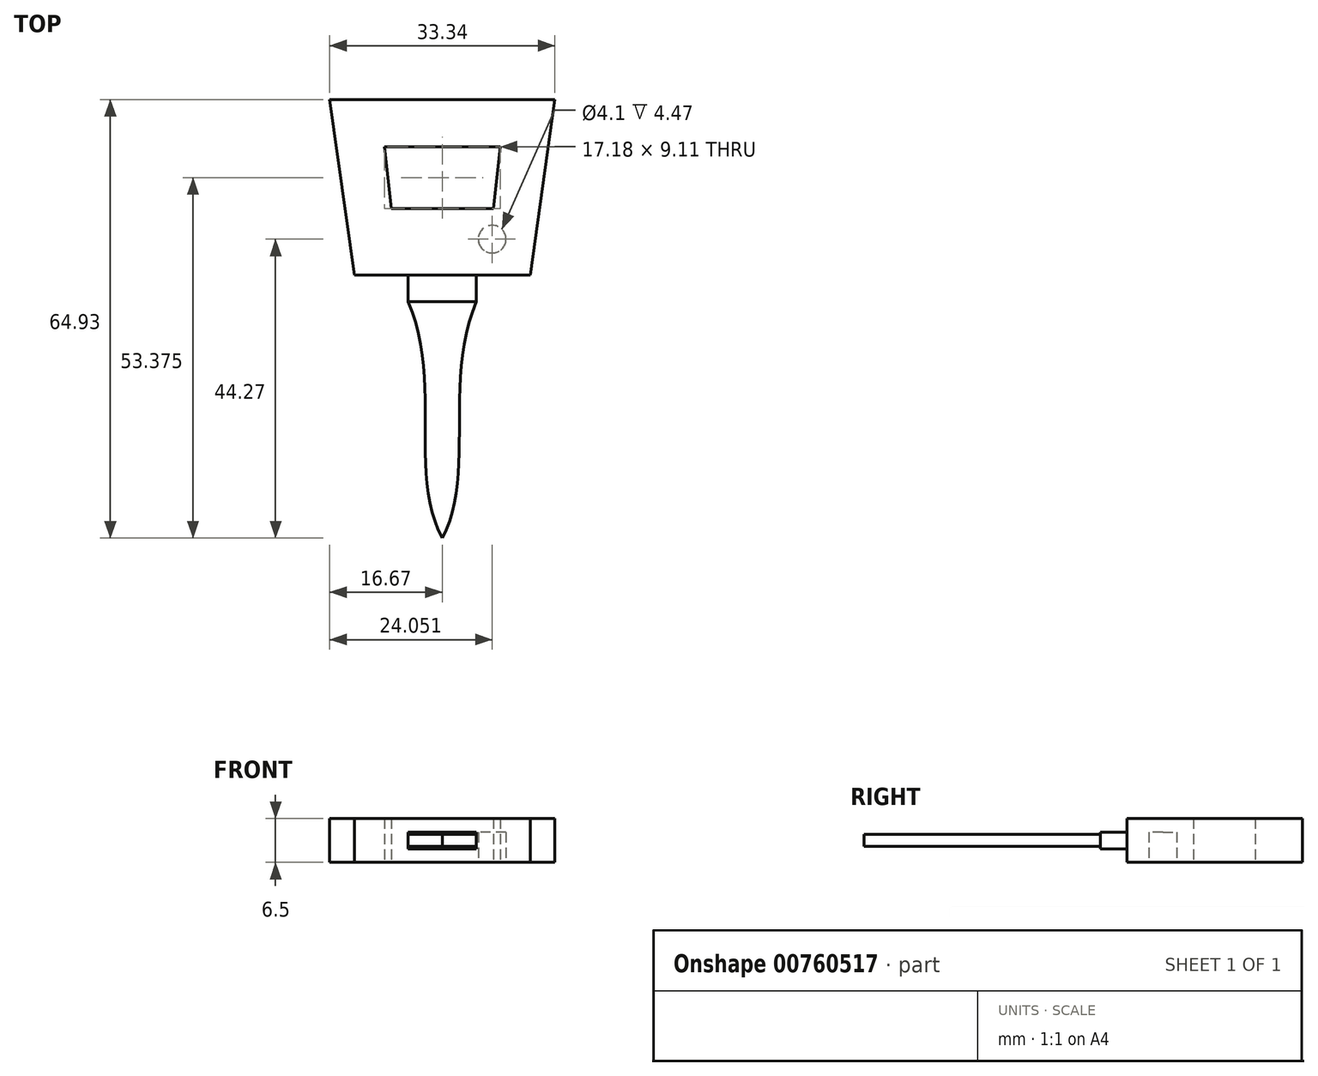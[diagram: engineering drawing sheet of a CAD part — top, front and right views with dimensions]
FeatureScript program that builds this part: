
annotation { "Feature Type Name" : "Feature", "Feature Type Description" : "" }
export const myFeature = defineFeature(function(context is Context, id is Id, definition is map)
    precondition{}
    {
        {
            var Q0;
            Q0=qCreatedBy(makeId("Top.planeOp"),FACE);
            var sketch = newSketch(context, id + "F0", { "sketchPlane" : qUnion([Q0])});
            skLineSegment(sketch, "E0.bottom", {"start": v(0, 0) * mm, "end": v(-5.04, 0) * mm});
            skLineSegment(sketch, "E0.left", {"start": v(0, 0) * mm, "end": v(0, -35) * mm});
            skLineSegment(sketch, "E1", {"start": v(-5.04, 0) * mm, "end": v(-5.04, 5.63) * mm});
            skLineSegment(sketch, "E2", {"start": v(-5.04, 5.63) * mm, "end": v(-10.67, 5.63) * mm});
            skPoint(sketch, "E3", {"position": v(0, 12.71) * mm});
            skLineSegment(sketch, "E4", {"start": v(0, 12.71) * mm, "end": v(-11.44, 12.71) * mm});
            skLineSegment(sketch, "E5", {"start": v(-12.47, 11.46) * mm, "end": v(-11.49, 6.3) * mm});
            skPoint(sketch, "E6", {"position": v(0, -35) * mm});
            skFitSpline(sketch, "E7", {"points": [v(0, -35) * mm, v(-5.04, 0) * mm], "startDerivative": vector(-15.12, 27.9) * mm, "endDerivative": vector(-15.12, 35.18) * mm});
            skLineSegment(sketch, "E8", {"start": v(0, 12.71) * mm, "end": v(0, -35) * mm, "construction": true});
            skFitSpline(sketch, "E9.MirrorCS", {"points": [v(0, -35) * mm, v(5.04, 0) * mm], "startDerivative": vector(15.12, 27.9) * mm, "endDerivative": vector(15.12, 35.18) * mm});
            skLineSegment(sketch, "E10.MirrorCS", {"start": v(5.04, 0) * mm, "end": v(5.04, 5.63) * mm});
            skLineSegment(sketch, "E11.MirrorCS", {"start": v(5.04, 5.63) * mm, "end": v(10.5, 5.63) * mm});
            skLineSegment(sketch, "E12.MirrorCS", {"start": v(12.47, 11.46) * mm, "end": v(11.52, 6.48) * mm});
            skLineSegment(sketch, "E13.MirrorCS", {"start": v(0, 12.71) * mm, "end": v(11.44, 12.71) * mm});
            skPoint(sketch, "E14", {"position": v(7.38, 9.27) * mm});
            skCircle(sketch, "E15", {"center": v(7.38, 9.27) * mm, "radius": 2.25 * mm});
            skLineSegment(sketch, "E16", {"start": v(0, 0) * mm, "end": v(5.04, 0) * mm});
            skArc(sketch, "E17.filletArc", {"start": v(-11.44, 12.71) * mm, "mid": v(-12.25, 12.33) * mm, "end": v(-12.47, 11.46) * mm});
            skArc(sketch, "E18.filletArc", {"start": v(12.47, 11.46) * mm, "mid": v(12.25, 12.33) * mm, "end": v(11.44, 12.71) * mm});
            skArc(sketch, "E19.filletArc", {"start": v(-11.49, 6.3) * mm, "mid": v(-11.2, 5.82) * mm, "end": v(-10.67, 5.63) * mm});
            skArc(sketch, "E20.filletArc", {"start": v(10.5, 5.63) * mm, "mid": v(11.16, 5.87) * mm, "end": v(11.52, 6.48) * mm});
            skSolve(sketch);
        }
        {
            var Q0;
            Q0=makeQuery(id+"F0.imprint","IMPRINT",FACE,{"disambiguationData":[TD([[makeQuery(id+"F0.imprint","IMPRINT",EDGE,{"derivedFrom":sQuery(id+"F0.wireOp",EDGE,"E0.bottom")}),-1.0]])]});
            extrude(context, id + "F1", {"entities" : qUnion([Q0]), "endBound" : BoundingType.SYMMETRIC, "depth" : 2.47 * mm, "offsetDistance" : 25 * mm});
        }
        {
            var Q0;
            Q0=makeQuery(id+"F0.imprint","IMPRINT",FACE,{"disambiguationData":[TD([[makeQuery(id+"F0.imprint","IMPRINT",EDGE,{"derivedFrom":sQuery(id+"F0.wireOp",EDGE,"E0.left")}),1.0]])]});
            var Q1;
            Q1=makeQuery(id+"F0.imprint","IMPRINT",FACE,{"disambiguationData":[TD([[makeQuery(id+"F0.imprint","IMPRINT",EDGE,{"derivedFrom":sQuery(id+"F0.wireOp",EDGE,"E0.bottom")}),1.0]])]});
            extrude(context, id + "F2", {"entities" : qUnion([Q0, Q1]), "operationType" : NewBodyOperationType.ADD, "endBound" : BoundingType.SYMMETRIC, "depth" : 1.75 * mm, "offsetDistance" : 25 * mm});
        }
        {
            var Q0;
            Q0=qCreatedBy(makeId("Top.planeOp"),FACE);
            var sketch = newSketch(context, id + "F3", { "sketchPlane" : qUnion([Q0])});
            skLineSegment(sketch, "E21.0", {"start": v(5.24, 0) * mm, "end": v(5.24, 5.43) * mm});
            skLineSegment(sketch, "E21.1", {"start": v(-12.67, 11.43) * mm, "end": v(-11.69, 6.27) * mm});
            skArc(sketch, "E21.2", {"start": v(-11.69, 6.27) * mm, "mid": v(-11.33, 5.67) * mm, "end": v(-10.67, 5.43) * mm});
            skLineSegment(sketch, "E21.3", {"start": v(-5.24, 5.43) * mm, "end": v(-10.67, 5.43) * mm});
            skLineSegment(sketch, "E21.4", {"start": v(-5.24, 0) * mm, "end": v(-5.24, 5.43) * mm});
            skArc(sketch, "E21.5", {"start": v(-11.44, 12.9) * mm, "mid": v(-12.4, 12.46) * mm, "end": v(-12.67, 11.43) * mm});
            skLineSegment(sketch, "E21.6", {"start": v(-11.44, 12.9) * mm, "end": v(11.44, 12.9) * mm});
            skArc(sketch, "E21.7", {"start": v(12.67, 11.43) * mm, "mid": v(12.4, 12.46) * mm, "end": v(11.44, 12.9) * mm});
            skLineSegment(sketch, "E21.8", {"start": v(12.67, 11.43) * mm, "end": v(11.72, 6.45) * mm});
            skArc(sketch, "E21.9", {"start": v(10.5, 5.43) * mm, "mid": v(11.29, 5.72) * mm, "end": v(11.72, 6.45) * mm});
            skLineSegment(sketch, "E21.10", {"start": v(5.24, 5.43) * mm, "end": v(10.5, 5.43) * mm});
            skCircle(sketch, "E22.0", {"center": v(7.38, 9.27) * mm, "radius": 2.05 * mm});
            skPoint(sketch, "E23", {"position": v(-5.24, 5.43) * mm});
            skPoint(sketch, "E24", {"position": v(5.24, 5.43) * mm});
            skLineSegment(sketch, "E25", {"start": v(-5.24, 0) * mm, "end": v(5.24, 0) * mm});
            skSolve(sketch);
        }
        {
            var Q0;
            Q0=qCreatedBy(makeId("Top.planeOp"),FACE);
            var sketch = newSketch(context, id + "F4", { "sketchPlane" : qUnion([Q0])});
            skLineSegment(sketch, "E26", {"start": v(0, 3.93) * mm, "end": v(-13, 3.93) * mm});
            skPoint(sketch, "E27.0", {"position": v(-5.24, 5.43) * mm});
            skPoint(sketch, "E27.1", {"position": v(5.24, 5.43) * mm});
            skLineSegment(sketch, "E28.0", {"start": v(-11.44, 12.9) * mm, "end": v(11.44, 12.9) * mm});
            skLineSegment(sketch, "E29.0", {"start": v(-12.67, 11.43) * mm, "end": v(-11.69, 6.27) * mm});
            skLineSegment(sketch, "E29.1", {"start": v(12.67, 11.43) * mm, "end": v(11.72, 6.45) * mm});
            skLineSegment(sketch, "E30", {"start": v(0, 3.93) * mm, "end": v(0, 29.93) * mm, "construction": true});
            skPoint(sketch, "E31", {"position": v(0, 29.93) * mm});
            skPoint(sketch, "E32", {"position": v(-16.67, 29.93) * mm});
            skLineSegment(sketch, "E33", {"start": v(-13, 3.93) * mm, "end": v(-16.67, 29.93) * mm});
            skLineSegment(sketch, "E34", {"start": v(-16.67, 29.93) * mm, "end": v(0, 29.93) * mm});
            skPoint(sketch, "E35", {"position": v(-7.56, 13.82) * mm});
            skPoint(sketch, "E36", {"position": v(-8.6, 22.93) * mm});
            skPoint(sketch, "E37", {"position": v(0, 22.93) * mm});
            skPoint(sketch, "E38", {"position": v(0, 13.82) * mm});
            skPoint(sketch, "E39", {"position": v(-13, 3.93) * mm});
            skPoint(sketch, "E40", {"position": v(0, 3.93) * mm});
            skCircle(sketch, "E41.0", {"center": v(7.38, 9.27) * mm, "radius": 2.05 * mm});
            skArc(sketch, "E42.0", {"start": v(-11.69, 6.27) * mm, "mid": v(-11.33, 5.67) * mm, "end": v(-10.67, 5.43) * mm});
            skArc(sketch, "E42.1", {"start": v(-11.44, 12.9) * mm, "mid": v(-12.4, 12.46) * mm, "end": v(-12.67, 11.43) * mm});
            skLineSegment(sketch, "E42.2", {"start": v(-5.24, 5.43) * mm, "end": v(-10.67, 5.43) * mm});
            skLineSegment(sketch, "E42.3", {"start": v(-5.24, 0) * mm, "end": v(-5.24, 5.43) * mm});
            skArc(sketch, "E42.4", {"start": v(12.67, 11.43) * mm, "mid": v(12.4, 12.46) * mm, "end": v(11.44, 12.9) * mm});
            skArc(sketch, "E42.5", {"start": v(10.5, 5.43) * mm, "mid": v(11.29, 5.72) * mm, "end": v(11.72, 6.45) * mm});
            skLineSegment(sketch, "E42.6", {"start": v(5.24, 5.43) * mm, "end": v(10.5, 5.43) * mm});
            skLineSegment(sketch, "E42.7", {"start": v(5.24, 0) * mm, "end": v(5.24, 5.43) * mm});
            skLineSegment(sketch, "E43", {"start": v(0, 13.82) * mm, "end": v(-7.56, 13.82) * mm});
            skLineSegment(sketch, "E44", {"start": v(-8.6, 22.93) * mm, "end": v(-7.56, 13.82) * mm});
            skLineSegment(sketch, "E45", {"start": v(-8.6, 22.93) * mm, "end": v(0, 22.93) * mm});
            skLineSegment(sketch, "E46.MirrorCS", {"start": v(16.67, 29.93) * mm, "end": v(0, 29.93) * mm});
            skLineSegment(sketch, "E47.MirrorCS", {"start": v(13, 3.93) * mm, "end": v(16.67, 29.93) * mm});
            skLineSegment(sketch, "E48.MirrorCS", {"start": v(0, 3.93) * mm, "end": v(13, 3.93) * mm});
            skLineSegment(sketch, "E49.MirrorCS", {"start": v(0, 13.82) * mm, "end": v(7.56, 13.82) * mm});
            skLineSegment(sketch, "E50.MirrorCS", {"start": v(8.6, 22.93) * mm, "end": v(7.56, 13.82) * mm});
            skLineSegment(sketch, "E51.MirrorCS", {"start": v(8.6, 22.93) * mm, "end": v(0, 22.93) * mm});
            skSolve(sketch);
        }
        {
            var Q0;
            Q0=makeQuery(id+"F4.imprint","IMPRINT",FACE,{"disambiguationData":[TD([[makeQuery(id+"F4.imprint","IMPRINT",EDGE,{"derivedFrom":sQuery(id+"F4.wireOp",EDGE,"E28.0")}),1.0]])]});
            extrude(context, id + "F5", {"entities" : qUnion([Q0]), "endBound" : BoundingType.SYMMETRIC, "depth" : 6.5 * mm, "offsetDistance" : 25 * mm});
        }
        {
            var Q0;
            Q0=makeQuery(id+"F5.opExtrude","CAP_FACE",FACE,{"disambiguationData":[OSD([sQuery(id+"F4.wireOp",EDGE,"E26"),sQuery(id+"F4.wireOp",EDGE,"E28.0"),sQuery(id+"F4.wireOp",EDGE,"E29.0"),sQuery(id+"F4.wireOp",EDGE,"E29.1"),sQuery(id+"F4.wireOp",EDGE,"E33"),sQuery(id+"F4.wireOp",EDGE,"E34"),sQuery(id+"F4.wireOp",EDGE,"E42.0"),sQuery(id+"F4.wireOp",EDGE,"E42.1"),sQuery(id+"F4.wireOp",EDGE,"E42.2"),sQuery(id+"F4.wireOp",EDGE,"E42.3"),sQuery(id+"F4.wireOp",EDGE,"E42.4"),sQuery(id+"F4.wireOp",EDGE,"E42.5"),sQuery(id+"F4.wireOp",EDGE,"E42.6"),sQuery(id+"F4.wireOp",EDGE,"E42.7"),sQuery(id+"F4.wireOp",EDGE,"E43"),sQuery(id+"F4.wireOp",EDGE,"E44"),sQuery(id+"F4.wireOp",EDGE,"E45"),sQuery(id+"F4.wireOp",EDGE,"E46.MirrorCS"),sQuery(id+"F4.wireOp",EDGE,"E47.MirrorCS"),sQuery(id+"F4.wireOp",EDGE,"E48.MirrorCS"),sQuery(id+"F4.wireOp",EDGE,"E49.MirrorCS"),sQuery(id+"F4.wireOp",EDGE,"E50.MirrorCS"),sQuery(id+"F4.wireOp",EDGE,"E51.MirrorCS")])],"isStart":false});
            var sketch = newSketch(context, id + "F6", { "sketchPlane" : qUnion([Q0])});
            skLineSegment(sketch, "E52.0", {"start": v(-11.44, 12.9) * mm, "end": v(11.44, 12.9) * mm});
            skArc(sketch, "E52.1", {"start": v(-11.44, 12.9) * mm, "mid": v(-12.4, 12.46) * mm, "end": v(-12.67, 11.43) * mm});
            skLineSegment(sketch, "E52.2", {"start": v(-12.67, 11.43) * mm, "end": v(-11.69, 6.27) * mm});
            skArc(sketch, "E52.3", {"start": v(-11.69, 6.27) * mm, "mid": v(-11.33, 5.67) * mm, "end": v(-10.67, 5.43) * mm});
            skLineSegment(sketch, "E52.4", {"start": v(-5.24, 5.43) * mm, "end": v(-10.67, 5.43) * mm});
            skArc(sketch, "E52.5", {"start": v(12.67, 11.43) * mm, "mid": v(12.4, 12.46) * mm, "end": v(11.44, 12.9) * mm});
            skLineSegment(sketch, "E52.6", {"start": v(12.67, 11.43) * mm, "end": v(11.72, 6.45) * mm});
            skArc(sketch, "E52.7", {"start": v(10.5, 5.43) * mm, "mid": v(11.29, 5.72) * mm, "end": v(11.72, 6.45) * mm});
            skLineSegment(sketch, "E52.8", {"start": v(5.24, 5.43) * mm, "end": v(10.5, 5.43) * mm});
            skLineSegment(sketch, "E53.0", {"start": v(5.24, 3.93) * mm, "end": v(5.24, 5.43) * mm});
            skLineSegment(sketch, "E53.1", {"start": v(-5.24, 3.93) * mm, "end": v(-5.24, 5.43) * mm});
            skLineSegment(sketch, "E54", {"start": v(-5.24, 3.93) * mm, "end": v(5.24, 3.93) * mm});
            skSolve(sketch);
        }
        {
            var Q0;
            Q0=makeQuery(id+"F6.imprint","IMPRINT",FACE,{"disambiguationData":[TD([[makeQuery(id+"F6.imprint","IMPRINT",EDGE,{"derivedFrom":sQuery(id+"F6.wireOp",EDGE,"E52.0")}),-1.0]])]});
            extrude(context, id + "F7", {"entities" : qUnion([Q0]), "operationType" : NewBodyOperationType.ADD, "oppositeDirection" : true, "depth" : 2.03 * mm, "offsetDistance" : 25 * mm});
        }
        {
            var Q0;
            Q0=makeQuery(id+"F5.opExtrude","CAP_FACE",FACE,{"disambiguationData":[OSD([sQuery(id+"F4.wireOp",EDGE,"E26"),sQuery(id+"F4.wireOp",EDGE,"E28.0"),sQuery(id+"F4.wireOp",EDGE,"E29.0"),sQuery(id+"F4.wireOp",EDGE,"E29.1"),sQuery(id+"F4.wireOp",EDGE,"E33"),sQuery(id+"F4.wireOp",EDGE,"E34"),sQuery(id+"F4.wireOp",EDGE,"E42.0"),sQuery(id+"F4.wireOp",EDGE,"E42.1"),sQuery(id+"F4.wireOp",EDGE,"E42.2"),sQuery(id+"F4.wireOp",EDGE,"E42.3"),sQuery(id+"F4.wireOp",EDGE,"E42.4"),sQuery(id+"F4.wireOp",EDGE,"E42.5"),sQuery(id+"F4.wireOp",EDGE,"E42.6"),sQuery(id+"F4.wireOp",EDGE,"E42.7"),sQuery(id+"F4.wireOp",EDGE,"E43"),sQuery(id+"F4.wireOp",EDGE,"E44"),sQuery(id+"F4.wireOp",EDGE,"E45"),sQuery(id+"F4.wireOp",EDGE,"E46.MirrorCS"),sQuery(id+"F4.wireOp",EDGE,"E47.MirrorCS"),sQuery(id+"F4.wireOp",EDGE,"E48.MirrorCS"),sQuery(id+"F4.wireOp",EDGE,"E49.MirrorCS"),sQuery(id+"F4.wireOp",EDGE,"E50.MirrorCS"),sQuery(id+"F4.wireOp",EDGE,"E51.MirrorCS")])],"isStart":true});
            var sketch = newSketch(context, id + "F8", { "sketchPlane" : qUnion([Q0])});
            skLineSegment(sketch, "E55.0", {"start": v(-11.44, -12.9) * mm, "end": v(11.44, -12.9) * mm});
            skArc(sketch, "E55.1", {"start": v(-11.44, -12.9) * mm, "mid": v(-12.4, -12.46) * mm, "end": v(-12.67, -11.43) * mm});
            skLineSegment(sketch, "E55.2", {"start": v(-12.67, -11.43) * mm, "end": v(-11.69, -6.27) * mm});
            skArc(sketch, "E55.3", {"start": v(-11.69, -6.27) * mm, "mid": v(-11.33, -5.67) * mm, "end": v(-10.67, -5.43) * mm});
            skLineSegment(sketch, "E55.4", {"start": v(-5.24, -5.43) * mm, "end": v(-10.67, -5.43) * mm});
            skArc(sketch, "E55.5", {"start": v(12.67, -11.43) * mm, "mid": v(12.4, -12.46) * mm, "end": v(11.44, -12.9) * mm});
            skLineSegment(sketch, "E55.6", {"start": v(12.67, -11.43) * mm, "end": v(11.72, -6.45) * mm});
            skArc(sketch, "E55.7", {"start": v(10.5, -5.43) * mm, "mid": v(11.29, -5.72) * mm, "end": v(11.72, -6.45) * mm});
            skLineSegment(sketch, "E55.8", {"start": v(5.24, -5.43) * mm, "end": v(10.5, -5.43) * mm});
            skLineSegment(sketch, "E55.9", {"start": v(5.24, -3.93) * mm, "end": v(5.24, -5.43) * mm});
            skLineSegment(sketch, "E55.10", {"start": v(-5.24, -3.93) * mm, "end": v(-5.24, -5.43) * mm});
            skLineSegment(sketch, "E55.11", {"start": v(-5.24, -3.93) * mm, "end": v(5.24, -3.93) * mm});
            skCircle(sketch, "E56.0", {"center": v(7.38, -9.27) * mm, "radius": 2.05 * mm});
            skSolve(sketch);
        }
        {
            var Q0;
            Q0=makeQuery(id+"F8.imprint","IMPRINT",FACE,{"disambiguationData":[TD([[makeQuery(id+"F8.imprint","IMPRINT",EDGE,{"derivedFrom":sQuery(id+"F8.wireOp",EDGE,"E55.0")}),1.0]])]});
            extrude(context, id + "F9", {"entities" : qUnion([Q0]), "operationType" : NewBodyOperationType.ADD, "oppositeDirection" : true, "depth" : 2.03 * mm, "offsetDistance" : 25 * mm});
        }
        {
            var Q0;
            Q0=makeQuery(id+"F8.imprint","IMPRINT",FACE,{"disambiguationData":[TD([[makeQuery(id+"F8.imprint","IMPRINT",EDGE,{"derivedFrom":sQuery(id+"F8.wireOp",EDGE,"E56.0")}),-1.0]])]});
            extrude(context, id + "F10", {"entities" : qUnion([Q0]), "operationType" : NewBodyOperationType.ADD, "oppositeDirection" : true, "depth" : 4.5 * mm, "offsetDistance" : 25 * mm});
        }
    });
